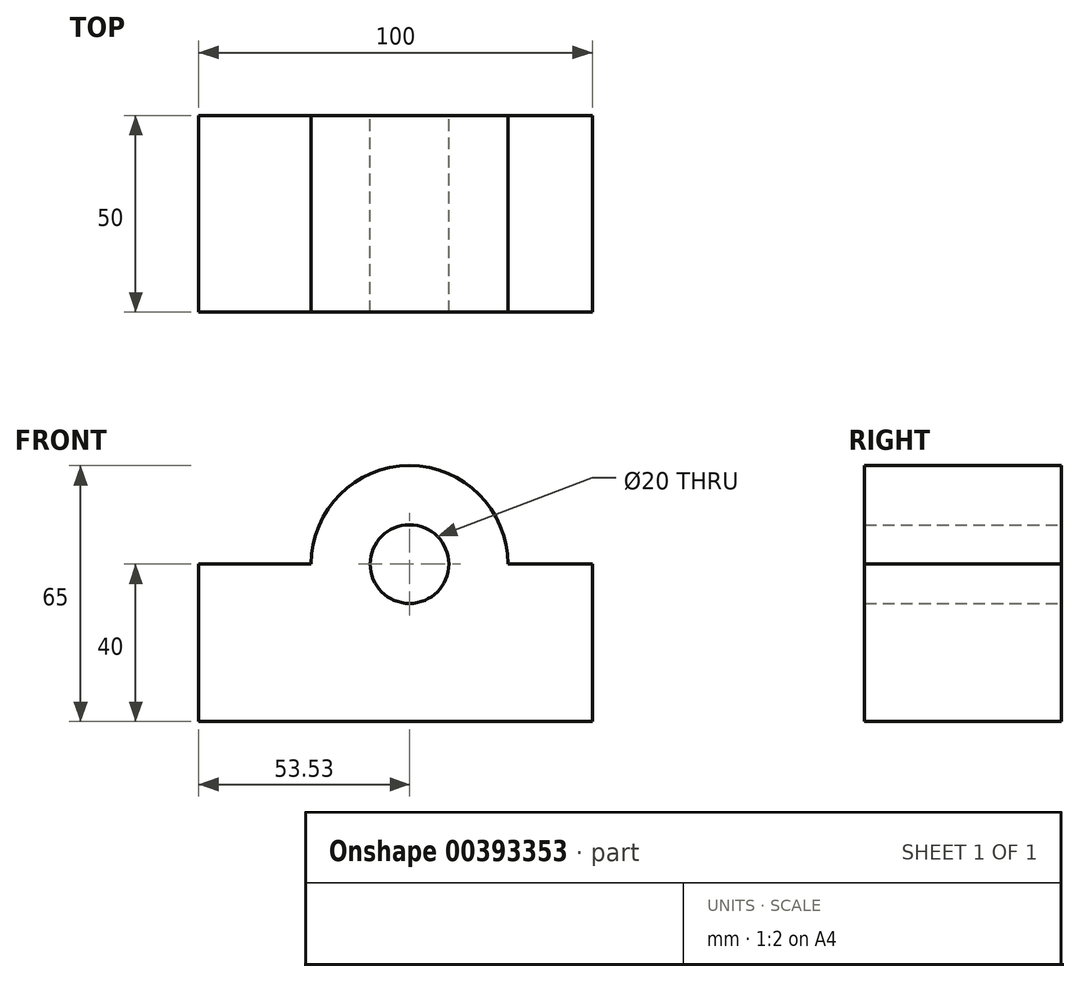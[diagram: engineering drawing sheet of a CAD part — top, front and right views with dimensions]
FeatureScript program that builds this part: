
annotation { "Feature Type Name" : "Feature", "Feature Type Description" : "" }
export const myFeature = defineFeature(function(context is Context, id is Id, definition is map)
    precondition{}
    {
        {
            var Q0;
            Q0=qCreatedBy(makeId("Front.planeOp"),FACE);
            var sketch = newSketch(context, id + "F0", { "sketchPlane" : qUnion([Q0])});
            skLineSegment(sketch, "E0.top", {"start": v(-53.53, -20) * mm, "end": v(46.47, -20) * mm});
            skLineSegment(sketch, "E0.left", {"start": v(-53.53, 20) * mm, "end": v(-53.53, -20) * mm});
            skLineSegment(sketch, "E0.right", {"start": v(46.47, 20) * mm, "end": v(46.47, -20) * mm});
            skArc(sketch, "E1", {"start": v(25, 20) * mm, "mid": v(0, 45) * mm, "end": v(-25, 20) * mm});
            skPoint(sketch, "E2", {"position": v(-53.53, 0) * mm});
            skLineSegment(sketch, "E3", {"start": v(-53.53, 20) * mm, "end": v(-25, 20) * mm});
            skLineSegment(sketch, "E4", {"start": v(25, 20) * mm, "end": v(46.47, 20) * mm});
            skCircle(sketch, "E5", {"center": v(0, 20) * mm, "radius": 10 * mm});
            skSolve(sketch);
        }
        {
            var Q0;
            Q0 = qSketchRegion(id + "F0", true);
            extrude(context, id + "F1", {"entities" : qUnion([Q0]), "depth" : 25 * mm});
        }
        {
            var Q0;
            Q0 = qSketchRegion(id + "F0", true);
            extrude(context, id + "F2", {"entities" : qUnion([Q0]), "operationType" : NewBodyOperationType.ADD, "depth" : 25 * mm, "hasSecondDirection" : true, "secondDirectionOppositeDirection" : true, "secondDirectionDepth" : 25 * mm});
        }
    });
